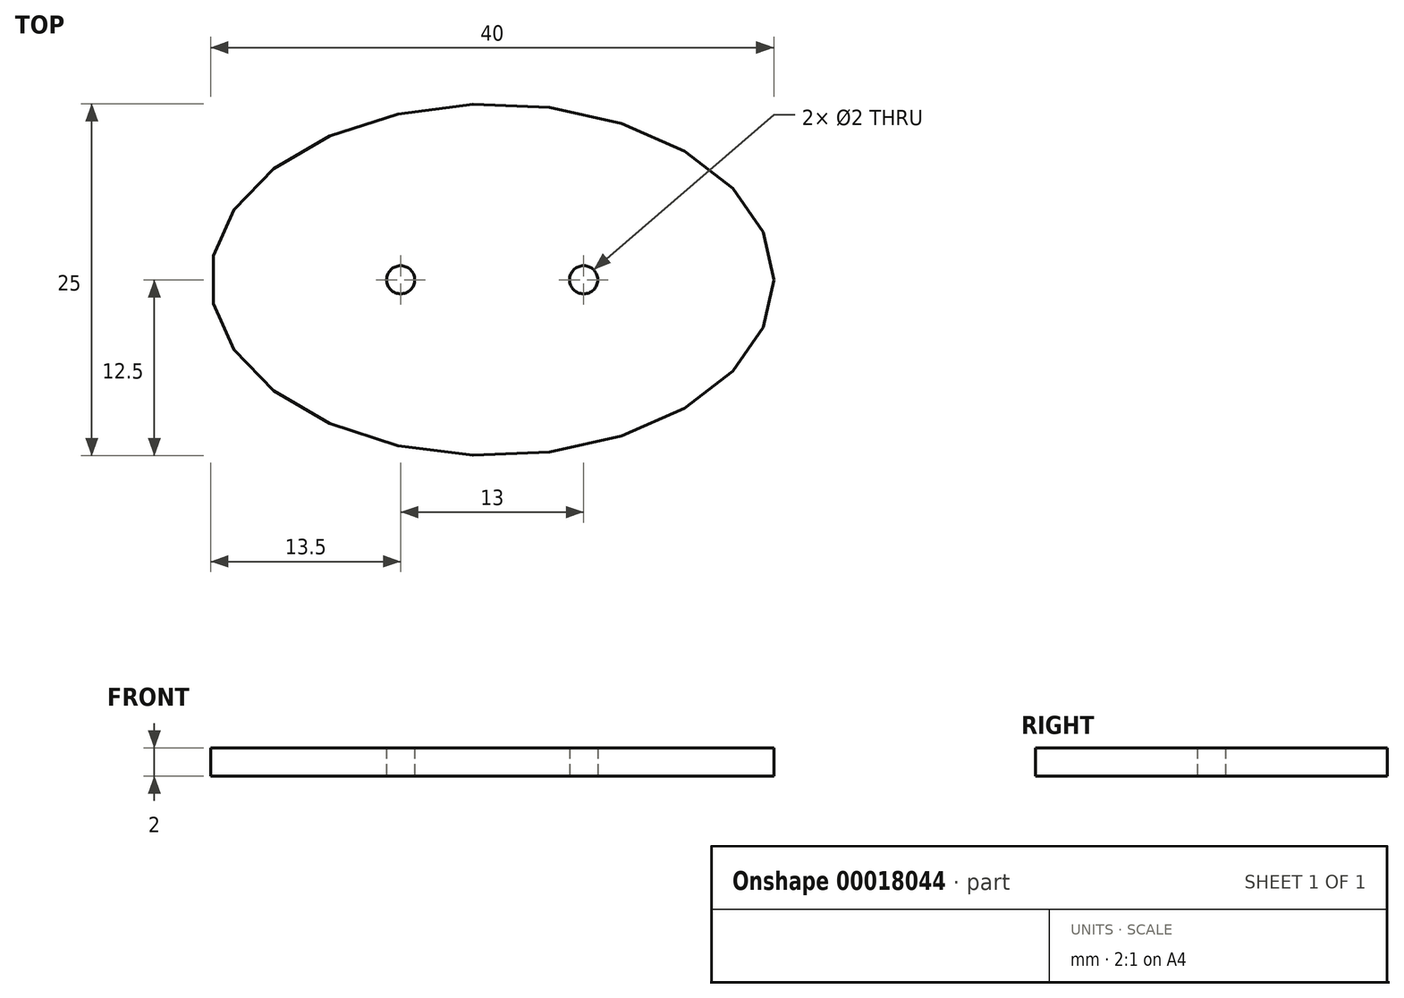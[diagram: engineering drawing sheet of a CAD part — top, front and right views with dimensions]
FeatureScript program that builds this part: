
annotation { "Feature Type Name" : "Feature", "Feature Type Description" : "" }
export const myFeature = defineFeature(function(context is Context, id is Id, definition is map)
    precondition{}
    {
        {
            var Q0;
            Q0=qCreatedBy(makeId("Top.planeOp"),FACE);
            var sketch = newSketch(context, id + "F0", { "sketchPlane" : qUnion([Q0])});
            skCircle(sketch, "E0", {"center": v(0, 0) * mm, "radius": 9.5 * mm, "construction": true});
            skCircle(sketch, "E1", {"center": v(13, 0) * mm, "radius": 3.5 * mm, "construction": true});
            skLineSegment(sketch, "E2", {"start": v(0, 0) * mm, "end": v(13, 0) * mm, "construction": true});
            skPoint(sketch, "E3", {"position": v(6.5, 0) * mm});
            skCircle(sketch, "E4", {"center": v(0, 0) * mm, "radius": 1 * mm});
            skCircle(sketch, "E5", {"center": v(13, 0) * mm, "radius": 1 * mm});
            skEllipse(sketch, "E6", {"center": v(6.5, 0) * mm, "majorRadius": 20 * mm, "minorRadius": 12.5 * mm, "majorAxis": v(1, 0)});
            skSolve(sketch);
        }
        {
            var Q0;
            Q0 = qSketchRegion(id + "F0", true);
            extrude(context, id + "F1", {"entities" : qUnion([Q0]), "depth" : 2 * mm});
        }
    });
